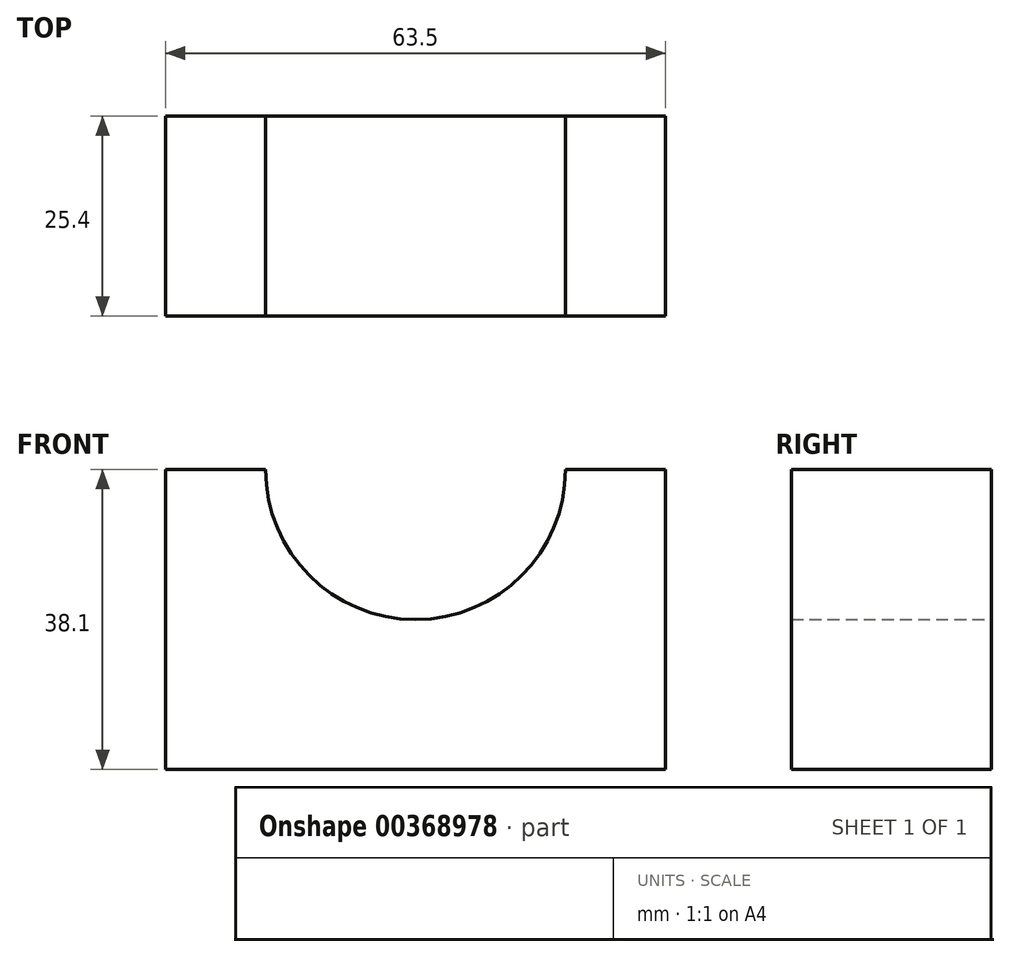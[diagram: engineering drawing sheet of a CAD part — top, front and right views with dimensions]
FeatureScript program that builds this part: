
annotation { "Feature Type Name" : "Feature", "Feature Type Description" : "" }
export const myFeature = defineFeature(function(context is Context, id is Id, definition is map)
    precondition{}
    {
        {
            var Q0;
            Q0=qCreatedBy(makeId("Front.planeOp"),FACE);
            var sketch = newSketch(context, id + "F0", { "sketchPlane" : qUnion([Q0])});
            skLineSegment(sketch, "E0", {"start": v(-63.5, 38.1) * mm, "end": v(-63.5, 0) * mm});
            skLineSegment(sketch, "E1", {"start": v(-63.5, 0) * mm, "end": v(0, 0) * mm});
            skLineSegment(sketch, "E2", {"start": v(0, 0) * mm, "end": v(0, 38.1) * mm});
            skLineSegment(sketch, "E3", {"start": v(-63.5, 38.1) * mm, "end": v(-50.8, 38.1) * mm});
            skLineSegment(sketch, "E4", {"start": v(0, 38.1) * mm, "end": v(-12.7, 38.1) * mm});
            skArc(sketch, "E5", {"start": v(-50.8, 38.1) * mm, "mid": v(-31.75, 19.05) * mm, "end": v(-12.7, 38.1) * mm});
            skSolve(sketch);
        }
        {
            var Q0;
            Q0=makeQuery(id+"F0.imprint","IMPRINT",FACE,{"disambiguationData":[TD([[makeQuery(id+"F0.imprint","IMPRINT",EDGE,{"derivedFrom":sQuery(id+"F0.wireOp",EDGE,"E0")}),1.0]])]});
            extrude(context, id + "F1", {"entities" : qUnion([Q0]), "depth" : 25.4 * mm});
        }
    });
